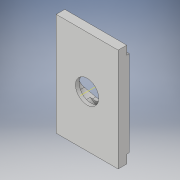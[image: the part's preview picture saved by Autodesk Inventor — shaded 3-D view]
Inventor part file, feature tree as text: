
AUTODESK INVENTOR PART (.ipt)
format: ipt  version: 2018 (Build 220112000, 112)  size: 382,464 bytes
history: native  units: mm
features: extrude x7, sketch x7, projected_geometry x5, other x1, pattern_circular x1
ambient origin geometry x8: Origin, YZ Plane, XZ Plane, XY Plane, X Axis, Y Axis, Z Axis, Center Point
bodies: Volumenkörper1 (feature_tree)
feature tree (21):
  extrude  "Extrusion1"  Depth=59.8mm
  extrude  "Extrusion2"  Depth=36.0mm
  extrude  "Extrusion3"  Depth=5.0mm
  extrude  "Extrusion4"  Depth=1.5mm TaperAngle=0.0deg
  extrude  "Extrusion5"  Depth=10.5mm
  other  "Arbeitsachse1"
  pattern_circular  "Runde Anordnung1"  [2 undecoded]
  extrude  "Extrusion6"  Depth=18.0mm
  extrude  "Extrusion7"  Depth=29.9mm
  sketch  "Skizze1"  dims[d0=36.0mm d1=59.8mm]
  sketch  "Skizze2"  dims[d2=5.0mm d3=0.0mm d4=36.0mm]
  sketch  "Skizze3"  dims[d5=5.0mm d6=5.0mm]
  projected_geometry  "Projizierte Kontur1"
  projected_geometry  "Projizierte Kontur2"
  projected_geometry  "Projizierte Kontur3"
  sketch  "Skizze4"  dims[d7=36.0mm d8=1.5mm d9=0.0mm]
  projected_geometry  "Projizierte Kontur4"
  sketch  "Skizze6"  dims[d10=13.5mm d11=10.5mm]
  projected_geometry  "Projizierte Kontur6"
  sketch  "Skizze7"  dims[d12=10.5mm]
  sketch  "Skizze8"  dims[d13=14.0mm d14=7.0mm d15=18.0mm d16=29.9mm d17=29.9mm d18=29.9mm d19=5.25mm d20=5.25mm d21=2.1mm d22=0.0mm d23=2.1mm d24=0.0mm d25=2.3mm d26=0.0mm d27=400.0mm d28=45.0deg d30=13.5mm d31=2.3mm d32=0.0mm d33=0.6mm d34=0.0mm]
note: 2 required parameter values undecoded (feature->parameter linkage not recoverable at this tier; creation-order binding heuristic only, values carry confidence <= 0.55)
